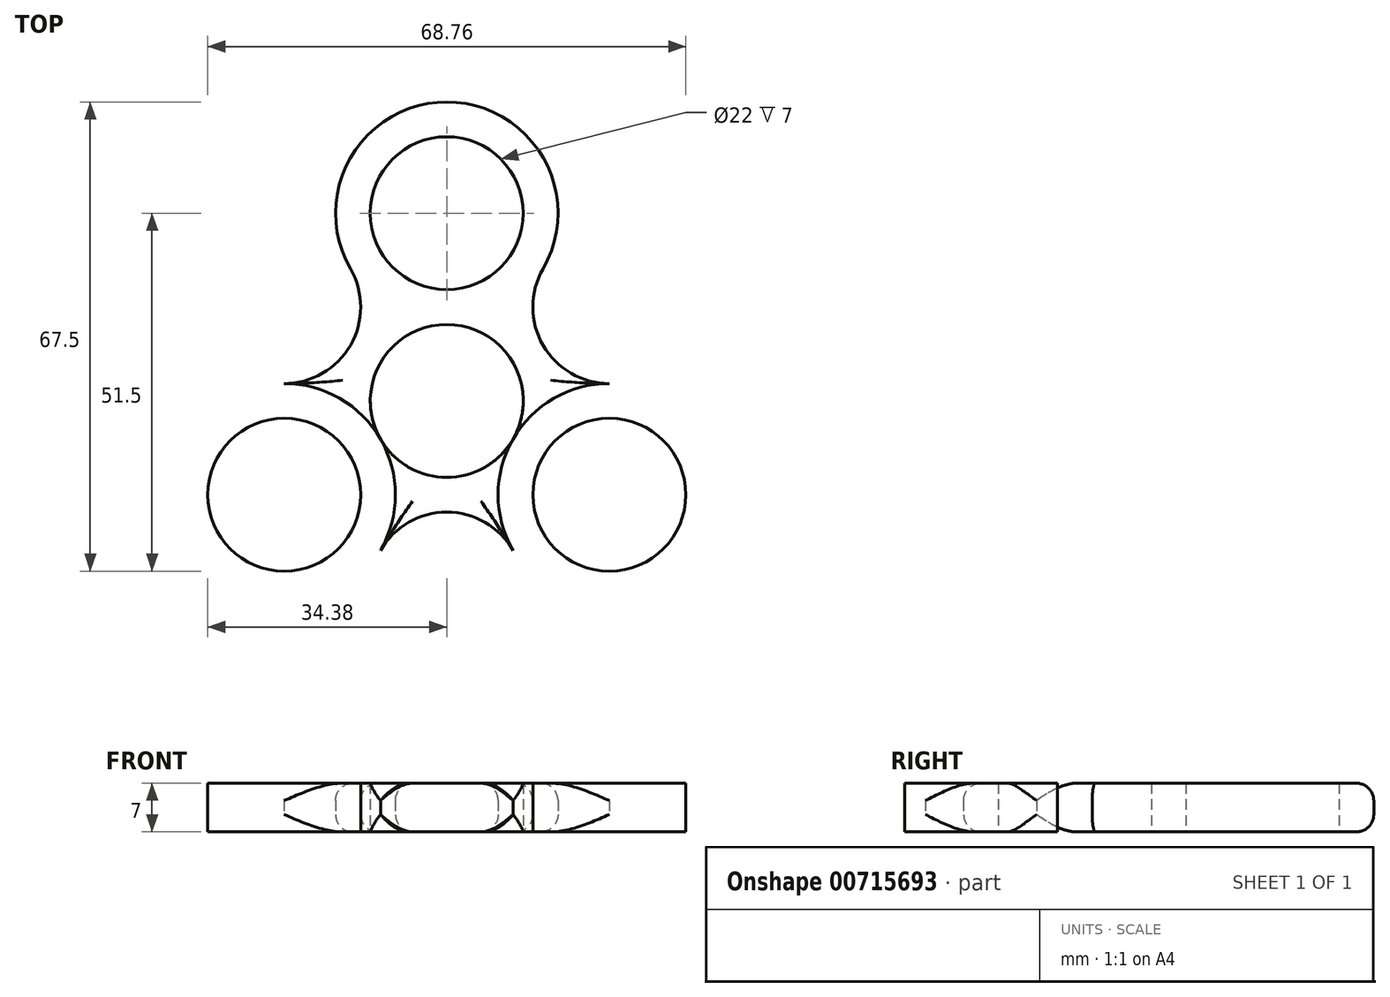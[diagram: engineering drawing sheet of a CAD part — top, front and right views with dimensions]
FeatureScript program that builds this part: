
annotation { "Feature Type Name" : "Feature", "Feature Type Description" : "" }
export const myFeature = defineFeature(function(context is Context, id is Id, definition is map)
    precondition{}
    {
        {
            var Q0;
            Q0=qCreatedBy(makeId("Top.planeOp"),FACE);
            var sketch = newSketch(context, id + "F0", { "sketchPlane" : qUnion([Q0])});
            skCircle(sketch, "E0", {"center": v(0, 0) * mm, "radius": 11 * mm});
            skCircle(sketch, "E1", {"center": v(0, 27) * mm, "radius": 11 * mm});
            skLineSegment(sketch, "E2", {"start": v(0, 0) * mm, "end": v(-39.98, 23.08) * mm, "construction": true});
            skLineSegment(sketch, "E3.MirrorCS", {"start": v(0, 0) * mm, "end": v(39.98, 23.08) * mm, "construction": true});
            skCircle(sketch, "E4.MirrorC", {"center": v(-23.38, -13.5) * mm, "radius": 11 * mm});
            skCircle(sketch, "E5.MirrorC", {"center": v(23.38, -13.5) * mm, "radius": 11 * mm});
            skLineSegment(sketch, "E6", {"start": v(0, 0) * mm, "end": v(0, -50.92) * mm, "construction": true});
            skCircle(sketch, "E7", {"center": v(-23.38, 13.5) * mm, "radius": 11 * mm});
            skCircle(sketch, "E8.MirrorC", {"center": v(23.38, 13.5) * mm, "radius": 11 * mm});
            skLineSegment(sketch, "E9.MirrorCS", {"start": v(0, 0) * mm, "end": v(39.98, -23.08) * mm, "construction": true});
            skCircle(sketch, "E10.MirrorC", {"center": v(0, -27) * mm, "radius": 11 * mm});
            skCircle(sketch, "E11", {"center": v(0, 27) * mm, "radius": 16 * mm});
            skCircle(sketch, "E12.MirrorC", {"center": v(23.38, -13.5) * mm, "radius": 16 * mm});
            skCircle(sketch, "E13.MirrorC", {"center": v(-23.38, -13.5) * mm, "radius": 16 * mm});
            skSolve(sketch);
        }
        {
            var Q0;
            Q0=makeQuery(id+"F0.imprint","IMPRINT",FACE,{"disambiguationData":[TD([[makeQuery(id+"F0.imprint","IMPRINT",EDGE,{"derivedFrom":sQuery(id+"F0.wireOp",EDGE,"E1")}),-1.0]])]});
            var Q1;
            Q1=makeQuery(id+"F0.imprint","IMPRINT",FACE,{"disambiguationData":[TD([[makeQuery(id+"F0.imprint","IMPRINT",EDGE,{"derivedFrom":sQuery(id+"F0.wireOp",EDGE,"E0")}),-1.0]])]});
            var Q2;
            Q2=makeQuery(id+"F0.imprint","IMPRINT",FACE,{"disambiguationData":[TD([[makeQuery(id+"F0.imprint","IMPRINT",EDGE,{"derivedFrom":sQuery(id+"F0.wireOp",EDGE,"E4.MirrorC")}),1.0]])]});
            var Q3;
            Q3=makeQuery(id+"F0.imprint","IMPRINT",FACE,{"disambiguationData":[TD([[makeQuery(id+"F0.imprint","IMPRINT",EDGE,{"derivedFrom":sQuery(id+"F0.wireOp",EDGE,"E5.MirrorC")}),1.0]])]});
            extrude(context, id + "F1", {"entities" : qUnion([Q0, Q1, Q2, Q3]), "depth" : 7 * mm, "offsetDistance" : 25 * mm});
        }
        {
            var Q0;
            Q0=makeQuery(id+"F1.opExtrude","CAP_EDGE",EDGE,{"disambiguationData":[OSD([sQuery(id+"F0.wireOp",EDGE,"E11")])],"isStart":false});
            var Q1;
            Q1=makeQuery(id+"F1.opExtrude","CAP_EDGE",EDGE,{"disambiguationData":[OSD([sQuery(id+"F0.wireOp",EDGE,"E11")])],"isStart":true});
            var Q2;
            Q2=makeQuery(id+"F1.opExtrude","CAP_EDGE",EDGE,{"disambiguationData":[OSD([sQuery(id+"F0.wireOp",EDGE,"E8.MirrorC")])],"isStart":false});
            var Q3;
            Q3=makeQuery(id+"F1.opExtrude","CAP_EDGE",EDGE,{"disambiguationData":[OSD([sQuery(id+"F0.wireOp",EDGE,"E8.MirrorC")])],"isStart":true});
            var Q4;
            Q4=makeQuery(id+"F1.opExtrude","CAP_EDGE",EDGE,{"disambiguationData":[OSD([sQuery(id+"F0.wireOp",EDGE,"E12.MirrorC")])],"isStart":true});
            var Q5;
            Q5=makeQuery(id+"F1.opExtrude","CAP_EDGE",EDGE,{"disambiguationData":[OSD([sQuery(id+"F0.wireOp",EDGE,"E12.MirrorC")])],"isStart":false});
            var Q6;
            Q6=makeQuery(id+"F1.opExtrude","CAP_EDGE",EDGE,{"disambiguationData":[OSD([sQuery(id+"F0.wireOp",EDGE,"E10.MirrorC")])],"isStart":false});
            var Q7;
            Q7=makeQuery(id+"F1.opExtrude","CAP_EDGE",EDGE,{"disambiguationData":[OSD([sQuery(id+"F0.wireOp",EDGE,"E10.MirrorC")])],"isStart":true});
            var Q8;
            Q8=makeQuery(id+"F1.opExtrude","CAP_EDGE",EDGE,{"disambiguationData":[OSD([sQuery(id+"F0.wireOp",EDGE,"E13.MirrorC")])],"isStart":true});
            var Q9;
            Q9=makeQuery(id+"F1.opExtrude","CAP_EDGE",EDGE,{"disambiguationData":[OSD([sQuery(id+"F0.wireOp",EDGE,"E13.MirrorC")])],"isStart":false});
            var Q10;
            Q10=makeQuery(id+"F1.opExtrude","CAP_EDGE",EDGE,{"disambiguationData":[OSD([sQuery(id+"F0.wireOp",EDGE,"E7")])],"isStart":false});
            var Q11;
            Q11=makeQuery(id+"F1.opExtrude","CAP_EDGE",EDGE,{"disambiguationData":[OSD([sQuery(id+"F0.wireOp",EDGE,"E7")])],"isStart":true});
            fillet(context, id + "F2", {"entities" : qUnion([Q0, Q1, Q2, Q3, Q4, Q5, Q6, Q7, Q8, Q9, Q10, Q11]), "radius" : 2.5 * mm, "tangentPropagation" : true, "allowEdgeOverflow" : false});
        }
    });
